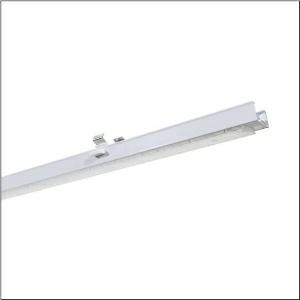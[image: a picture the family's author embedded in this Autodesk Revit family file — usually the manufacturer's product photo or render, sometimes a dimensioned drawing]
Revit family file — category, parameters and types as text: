
# Revit family: sanierungs-leuchteneinsatz_31_gen_2_51re12db4cb_add1
name_source: partatom
category: Lighting Fixtures
units: mm (PartAtom-declared; Revit-internal decimal feet)

## family parameters
Cut with Voids When Loaded = No
Host = Face
Light Source = No
Part Type = Normal
Room Calculation Point = No
Round Connector Dimension = Use Diameter
Shared = No

## types (1)
- Sanierungs-Leuchteneinsatz 31 Gen.2 (1 x LED, 11500 lm, 66 W, 4000K)
    Apparent Load = 66 VA
    CIE Flux Codes = 65 91 98 99 100
    Color Rendering = 80
    Color Temperature = 4000K
    Default Elevation = 1800 mm
    Description = Refurbishment luminaire insert Gen.2, luminaire insert, of extruded aluminium section, coated, traffic white (RAL 9016), length: 1.472mm, width: 91mm, height: 53mm, LED rated luminous flux: 11.500lm, light colour: 840, control gear: DALI 2, with system connector: socket, mains connection: 220..240V, AC, 50/60Hz, primary light control with lens, of plastic, primary optical cover: cover, of PMMA, light emission: direct distribution, protection rating (complete): IP20, insulation class (complete): insulation class I (protective earthing), certification: CE, UKCA, impact resistance: IK02, permissible ambient temperature for indoor applications: -20..+40°C, packaging unit: 1 piece
    Height = 58 mm
    Lamp = 1 x LED
    Lamp Light Flux = 11500 lm
    Lamp Power = 66 W
    Lamp count = 1
    Length = 1472 mm
    Luminous efficacy = 174 lm/W
    Manufacturer = Siteco
    ModVariant = No
    Model = 51RE12DB4CB
    Mounting Place = Ceiling
    Mounting Type = Pendant
    Number of Poles = 1
    OnlyDefault = Yes
    Power Factor = 1
    Product Name = Sanierungs-Leuchteneinsatz 31 Gen.2
    Product group = luminaire insert
    ProductGroupID = 902
    Protection Class = Protection class I
    Protection Degree = IP 20
    RLX_Detail_Level = 1
    RlxData = <blob elided: 19517 chars, md5=b9c29a5a>
    Socket = socket
    Standby Power = 0 W
    System Light Flux = 11500 lm
    System Power = 66 W
    Type Comments = Product without accessories
    Type Image = l_1266702.jpg
    URL = http://relux.com
    VarID = ---
    Voltage = 0 V
    Weight = 0.00 kg
    Width = 65 mm

## geometry (parser evidence)
native form markers: Blend x4, Sweep x12
no freeform markers — native parametric forms only
